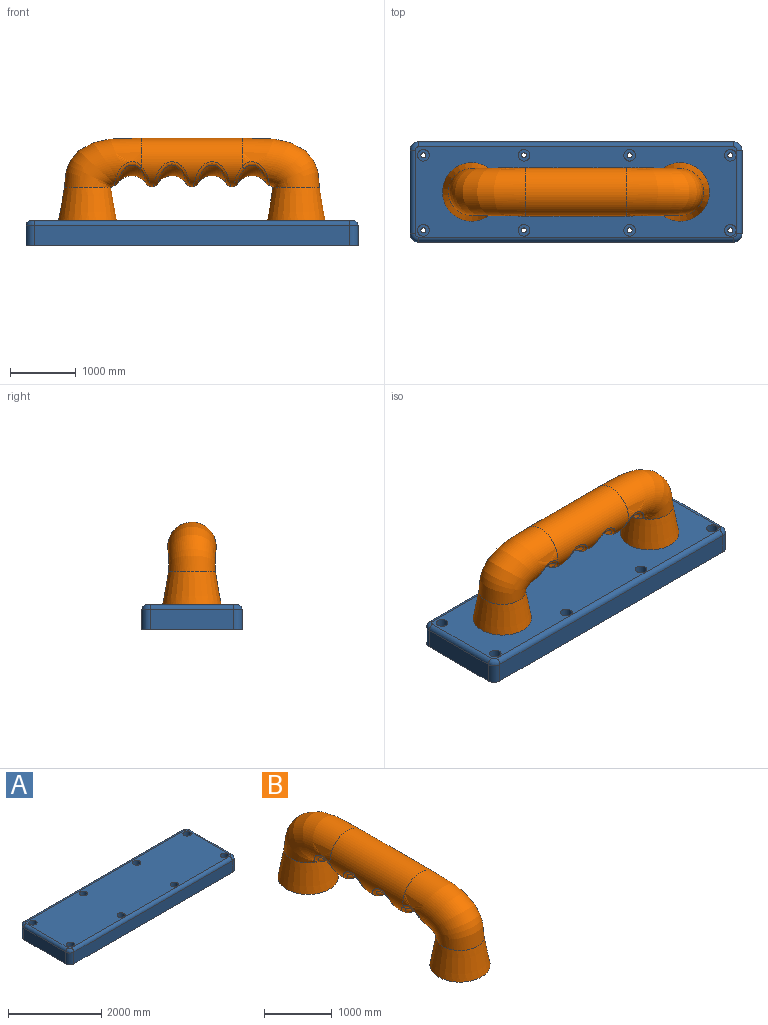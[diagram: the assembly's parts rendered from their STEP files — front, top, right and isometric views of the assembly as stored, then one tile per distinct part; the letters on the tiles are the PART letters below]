
ASSEMBLY  parts=2 mates=1
PART A: 42 faces, bbox 5054.6x1524x381 mm
  f0: plane 4902.2x1371.6mm, normal (0,0,1), area 6523012.9mm2, adj f14,f16,f18,f20,f22,f24,f26,f28
  f1: cylinder r=38.1mm len=254mm, axis (0,0,-1), area 60804.9mm2, adj f13,f19
  f2: cylinder r=38.1mm len=254mm, axis (0,0,-1), area 60804.9mm2, adj f13,f21
  f3: cylinder r=38.1mm len=254mm, axis (0,0,-1), area 60804.9mm2, adj f13,f25
  f4: cylinder r=38.1mm len=254mm, axis (0,0,-1), area 60804.9mm2, adj f13,f23
  f5: cylinder r=38.1mm len=254mm, axis (0,0,-1), area 60804.9mm2, adj f13,f27
  f6: cylinder r=38.1mm len=254mm, axis (0,0,-1), area 60804.9mm2, adj f13,f29
  f7: cylinder r=38.1mm len=254mm, axis (0,0,-1), area 60804.9mm2, adj f13,f15
  f8: cylinder r=38.1mm len=254mm, axis (0,0,-1), area 60804.9mm2, adj f13,f17
  f9: plane 4800.6x304.8mm, normal (0,1,0), area 1463222.9mm2, adj f13,f33,f34,f36
  f10: plane 1270x304.8mm, normal (-1,0,0), area 387096mm2, adj f13,f31,f34,f40
  f11: plane 4800.6x304.8mm, normal (0,-1,0), area 1463222.9mm2, adj f13,f30,f38,f40
  f12: plane 1270x304.8mm, normal (1,0,0), area 387096mm2, adj f13,f32,f36,f38
  f13: plane 5054.6x1524mm, normal (0,0,-1), area 7652882.2mm2, adj f1,f2,f3,f4,f5,f6,f7,f8
  f14: cylinder r=88.9mm len=177.8mm, axis (0,0,1), area 70939mm2, adj f0,f15
  f15: plane 177.8x177.8mm, normal (0,0,1), area 20268.3mm2, adj f7,f14
  f16: cylinder r=88.9mm len=177.8mm, axis (0,0,1), area 70939mm2, adj f0,f17
  f17: plane 177.8x177.8mm, normal (0,0,1), area 20268.3mm2, adj f8,f16
  f18: cylinder r=88.9mm len=177.8mm, axis (0,0,1), area 70939mm2, adj f0,f19
  f19: plane 177.8x177.8mm, normal (0,0,1), area 20268.3mm2, adj f1,f18
  f20: cylinder r=88.9mm len=177.8mm, axis (0,0,1), area 70939mm2, adj f0,f21
  f21: plane 177.8x177.8mm, normal (0,0,1), area 20268.3mm2, adj f2,f20
  f22: cylinder r=88.9mm len=177.8mm, axis (0,0,1), area 70939mm2, adj f0,f23
  f23: plane 177.8x177.8mm, normal (0,0,1), area 20268.3mm2, adj f4,f22
  f24: cylinder r=88.9mm len=177.8mm, axis (0,0,1), area 70939mm2, adj f0,f25
  f25: plane 177.8x177.8mm, normal (0,0,1), area 20268.3mm2, adj f3,f24
  f26: cylinder r=88.9mm len=177.8mm, axis (0,0,1), area 70939mm2, adj f0,f27
  f27: plane 177.8x177.8mm, normal (0,0,1), area 20268.3mm2, adj f5,f26
  f28: cylinder r=88.9mm len=177.8mm, axis (0,0,1), area 70939mm2, adj f0,f29
  f29: plane 177.8x177.8mm, normal (0,0,1), area 20268.3mm2, adj f6,f28
  f30: cylinder r=76.2mm len=4800.6mm, axis (-1,0,0), area 574606.3mm2, adj f0,f11,f39,f41
  f31: cylinder r=76.2mm len=1270mm, axis (0,1,0), area 152012.2mm2, adj f0,f10,f35,f41
  f32: cylinder r=76.2mm len=1270mm, axis (0,-1,0), area 152012.2mm2, adj f0,f12,f37,f39
  f33: cylinder r=76.2mm len=4800.6mm, axis (1,0,0), area 574606.3mm2, adj f0,f9,f35,f37
  f34: cylinder r=127mm len=304.8mm, axis (0,0,-1), area 60804.9mm2, adj f9,f10,f13,f35
  f35: torus R=50.8mm, axis (0,0,1), area 18671.9mm2, adj f0,f31,f33,f34
  f36: cylinder r=127mm len=304.8mm, axis (0,0,1), area 60804.9mm2, adj f9,f12,f13,f37
  f37: torus R=50.8mm, axis (0,0,1), area 18671.9mm2, adj f0,f32,f33,f36
  f38: cylinder r=127mm len=304.8mm, axis (0,0,-1), area 60804.9mm2, adj f11,f12,f13,f39
  f39: torus R=50.8mm, axis (0,0,1), area 18671.9mm2, adj f0,f30,f32,f38
  f40: cylinder r=127mm len=304.8mm, axis (0,0,1), area 60804.9mm2, adj f10,f11,f13,f41
  f41: torus R=50.8mm, axis (0,0,1), area 18671.9mm2, adj f0,f30,f31,f40
PART B: 17 faces, bbox 1179.8x4064x1257.8 mm
  f0: cylinder r=368.3mm len=1524mm, axis (0,1,0), area 2227630.4mm2, adj f1,f6,f11,f12,f14,f16
  f1: bspline ~1179.7x749.76mm, area 1955503mm2, adj f0,f2,f13
  f2: cone r=444.5mm half-angle=10deg, axis (0,0,-1), area 1295508.7mm2, adj f1,f3
  f3: plane 889x889mm, normal (0,0,-1), area 620716.7mm2, adj f2
  f4: cone r=444.5mm half-angle=10deg, axis (0,0,-1), area 1295508.7mm2, adj f5,f6
  f5: plane 889x889mm, normal (0,0,-1), area 620716.7mm2, adj f4
  f6: bspline ~1179.7x749.76mm, area 1955360.4mm2, adj f0,f4,f15
  f7: torus R=711.2mm, axis (0,1,0), area 342548.6mm2, adj f15,f16
  f8: torus R=711.2mm, axis (0,1,0), area 342652.9mm2, adj f13,f14
  f9: torus R=711.2mm, axis (0,1,0), area 348261.1mm2, adj f12
  f10: torus R=711.2mm, axis (0,1,0), area 348209.6mm2, adj f11
  f11: bspline ~738.07x571.93mm, area 179063.7mm2, adj f0,f10
  f12: bspline ~738.07x571.94mm, area 179124.8mm2, adj f0,f9
  f13: bspline ~736.04x421.31mm, area 97453.9mm2, adj f1,f8,f14
  f14: bspline ~725.97x305.8mm, area 72031.7mm2, adj f0,f8,f13
  f15: bspline ~736.04x421.31mm, area 97454.4mm2, adj f6,f7,f16
  f16: bspline ~725.97x305.8mm, area 72031.7mm2, adj f0,f7,f15
PLACE A t=(5961.02,2418.4,-4009.18)mm
PLACE B rot(axis=(0,0,1),90deg) t=(3534.99,1656.74,181.82)mm
MATE fastened B.f3 <-> A.f0  axis (0,0,1) through (3534.99,1656.74,181.82)mm
